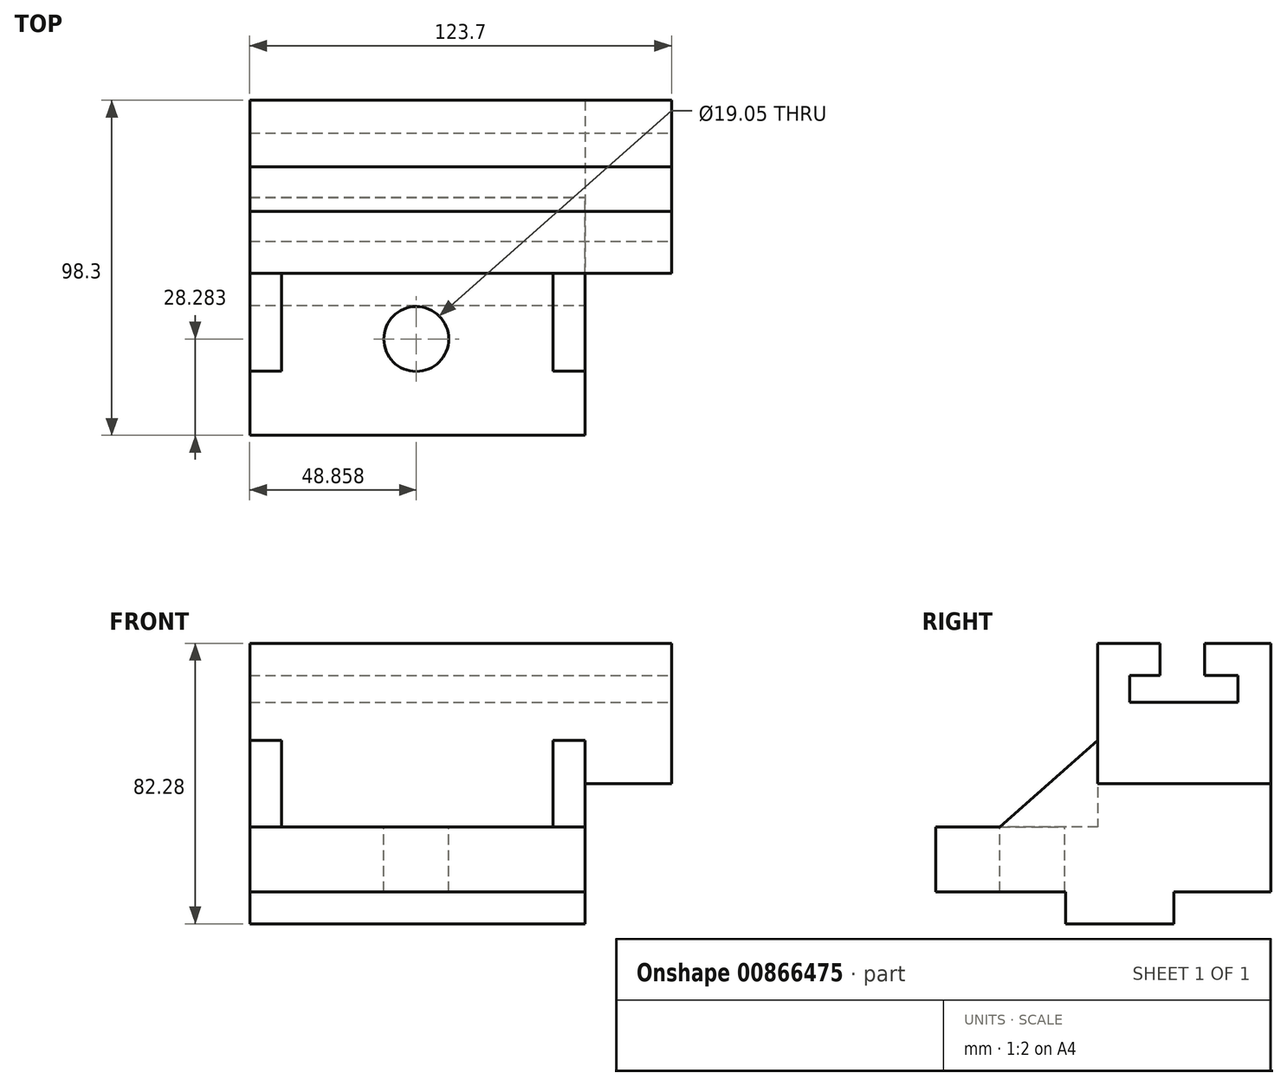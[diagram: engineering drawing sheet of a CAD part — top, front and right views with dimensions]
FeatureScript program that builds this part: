
annotation { "Feature Type Name" : "Feature", "Feature Type Description" : "" }
export const myFeature = defineFeature(function(context is Context, id is Id, definition is map)
    precondition{}
    {
        {
            var Q0;
            Q0=qCreatedBy(makeId("Top.planeOp"),FACE);
            var sketch = newSketch(context, id + "F0", { "sketchPlane" : qUnion([Q0])});
            skLineSegment(sketch, "E0.bottom", {"start": v(-46.6, 79.5) * mm, "end": v(51.7, 79.5) * mm});
            skLineSegment(sketch, "E0.top", {"start": v(-46.6, -18.8) * mm, "end": v(51.7, -18.8) * mm});
            skLineSegment(sketch, "E0.left", {"start": v(-46.6, 79.5) * mm, "end": v(-46.6, -18.8) * mm});
            skLineSegment(sketch, "E0.right", {"start": v(51.7, 79.5) * mm, "end": v(51.7, -18.8) * mm});
            skLineSegment(sketch, "E1", {"start": v(-46.6, 79.5) * mm, "end": v(-46.6, 30.35) * mm});
            skLineSegment(sketch, "E2", {"start": v(-46.6, 30.35) * mm, "end": v(-46.6, -1.4) * mm});
            skSolve(sketch);
        }
        {
            var Q0;
            Q0=makeQuery(id+"F0.imprint","IMPRINT",FACE,{"disambiguationData":[TD([[makeQuery(id+"F0.imprint","IMPRINT",EDGE,{"derivedFrom":sQuery(id+"F0.wireOp",EDGE,"E0.bottom")}),-1.0]])]});
            extrude(context, id + "F1", {"entities" : qUnion([Q0]), "depth" : 19.05 * mm, "offsetDistance" : 25.4 * mm});
        }
        {
            var Q0;
            Q0=makeQuery(id+"F1.opExtrude","SWEPT_FACE",FACE,{"disambiguationData":[OSD([sQuery(id+"F0.wireOp",EDGE,"E0.right")])]});
            var sketch = newSketch(context, id + "F2", { "sketchPlane" : qUnion([Q0])});
            skLineSegment(sketch, "E3", {"start": v(79.5, 0) * mm, "end": v(51.05, 0) * mm});
            skLineSegment(sketch, "E4", {"start": v(51.05, 0) * mm, "end": v(19.3, 0) * mm});
            skLineSegment(sketch, "E5", {"start": v(19.3, 0) * mm, "end": v(19.3, -9.38) * mm});
            skLineSegment(sketch, "E6", {"start": v(19.3, -9.38) * mm, "end": v(51.02, -9.38) * mm});
            skLineSegment(sketch, "E7", {"start": v(51.02, -9.38) * mm, "end": v(51.05, 0) * mm});
            skSolve(sketch);
        }
        {
            var Q0;
            Q0=makeQuery(id+"F2.imprint","IMPRINT",FACE,{"disambiguationData":[TD([[makeQuery(id+"F2.imprint","IMPRINT",EDGE,{"derivedFrom":sQuery(id+"F2.wireOp",EDGE,"E4")}),1.0]])]});
            extrude(context, id + "F3", {"entities" : qUnion([Q0]), "operationType" : NewBodyOperationType.ADD, "oppositeDirection" : true, "depth" : 98.3 * mm, "offsetDistance" : 25.4 * mm});
        }
        {
            var Q0;
            Q0=makeQuery(id+"F1.opExtrude","CAP_FACE",FACE,{"disambiguationData":[OSD([sQuery(id+"F0.wireOp",EDGE,"E0.bottom"),sQuery(id+"F0.wireOp",EDGE,"E0.top"),sQuery(id+"F0.wireOp",EDGE,"E0.left"),sQuery(id+"F0.wireOp",EDGE,"E0.right"),sQuery(id+"F0.wireOp",EDGE,"E1"),sQuery(id+"F0.wireOp",EDGE,"E2")])],"isStart":false});
            var sketch = newSketch(context, id + "F4", { "sketchPlane" : qUnion([Q0])});
            skLineSegment(sketch, "E8.bottom", {"start": v(-46.6, 79.5) * mm, "end": v(77.1, 79.5) * mm});
            skLineSegment(sketch, "E8.top", {"start": v(-46.6, 28.7) * mm, "end": v(77.1, 28.7) * mm});
            skLineSegment(sketch, "E8.left", {"start": v(-46.6, 79.5) * mm, "end": v(-46.6, 28.7) * mm});
            skLineSegment(sketch, "E8.right", {"start": v(77.1, 79.5) * mm, "end": v(77.1, 28.7) * mm});
            skSolve(sketch);
        }
        {
            var Q0;
            Q0 = qSketchRegion(id + "F4", true);
            extrude(context, id + "F5", {"entities" : qUnion([Q0]), "operationType" : NewBodyOperationType.ADD, "depth" : 53.85 * mm, "offsetDistance" : 25.4 * mm});
        }
        {
            var Q0;
            Q0=makeQuery(id+"F1.opExtrude","CAP_FACE",FACE,{"disambiguationData":[OSD([sQuery(id+"F0.wireOp",EDGE,"E0.bottom"),sQuery(id+"F0.wireOp",EDGE,"E0.top"),sQuery(id+"F0.wireOp",EDGE,"E0.left"),sQuery(id+"F0.wireOp",EDGE,"E0.right"),sQuery(id+"F0.wireOp",EDGE,"E1"),sQuery(id+"F0.wireOp",EDGE,"E2")])],"isStart":false});
            var sketch = newSketch(context, id + "F6", { "sketchPlane" : qUnion([Q0])});
            skLineSegment(sketch, "E9.bottom", {"start": v(51.7, 28.7) * mm, "end": v(42.3, 28.7) * mm});
            skLineSegment(sketch, "E9.top", {"start": v(51.7, 0) * mm, "end": v(42.3, 0) * mm});
            skLineSegment(sketch, "E9.left", {"start": v(51.7, 28.7) * mm, "end": v(51.7, 0) * mm});
            skLineSegment(sketch, "E9.right", {"start": v(42.3, 28.7) * mm, "end": v(42.3, 0) * mm});
            skSolve(sketch);
        }
        {
            var Q0;
            Q0 = qSketchRegion(id + "F6", true);
            extrude(context, id + "F7", {"entities" : qUnion([Q0]), "operationType" : NewBodyOperationType.ADD, "depth" : 25.4 * mm, "offsetDistance" : 25.4 * mm});
        }
        {
            var Q0;
            Q0=makeQuery(id+"F7.boolean.opBoolean","MERGE",FACE,{"derivedFrom":[makeQuery(id+"F3.boolean.opBoolean","MERGE",FACE,{"derivedFrom":[makeQuery(id+"F1.opExtrude","SWEPT_FACE",FACE,{"disambiguationData":[OSD([sQuery(id+"F0.wireOp",EDGE,"E0.right")])]}),makeQuery(id+"F3.opExtrude","CAP_FACE",FACE,{"disambiguationData":[OSD([sQuery(id+"F2.wireOp",EDGE,"E4"),sQuery(id+"F2.wireOp",EDGE,"E5"),sQuery(id+"F2.wireOp",EDGE,"E6"),sQuery(id+"F2.wireOp",EDGE,"E7")])],"isStart":true})]}),makeQuery(id+"F7.opExtrude","SWEPT_FACE",FACE,{"disambiguationData":[OSD([sQuery(id+"F6.wireOp",EDGE,"E9.left")])]})]});
            var sketch = newSketch(context, id + "F8", { "sketchPlane" : qUnion([Q0])});
            skLineSegment(sketch, "E10", {"start": v(0, 19.05) * mm, "end": v(28.7, 44.45) * mm});
            skSolve(sketch);
        }
        {
            var Q0;
            Q0 = qSketchRegion(id + "F8", true);
            var Q1;
            Q1=makeQuery(id+"F8.imprint","IMPRINT",FACE,{"disambiguationData":[TD([[makeQuery(id+"F8.imprint","IMPRINT",EDGE,{"derivedFrom":sQuery(id+"F8.wireOp",EDGE,"E10")}),1.0]])]});
            extrude(context, id + "F9", {"entities" : qUnion([Q0, Q1]), "operationType" : NewBodyOperationType.REMOVE, "oppositeDirection" : true, "depth" : 25.4 * mm, "offsetDistance" : 25.4 * mm});
        }
        {
            var Q0;
            Q0=makeQuery(id+"F1.opExtrude","CAP_FACE",FACE,{"disambiguationData":[OSD([sQuery(id+"F0.wireOp",EDGE,"E0.bottom"),sQuery(id+"F0.wireOp",EDGE,"E0.top"),sQuery(id+"F0.wireOp",EDGE,"E0.left"),sQuery(id+"F0.wireOp",EDGE,"E0.right"),sQuery(id+"F0.wireOp",EDGE,"E1"),sQuery(id+"F0.wireOp",EDGE,"E2")])],"isStart":false});
            var sketch = newSketch(context, id + "F10", { "sketchPlane" : qUnion([Q0])});
            skLineSegment(sketch, "E11.bottom", {"start": v(-46.6, 28.7) * mm, "end": v(-37.2, 28.7) * mm});
            skLineSegment(sketch, "E11.top", {"start": v(-46.6, 0) * mm, "end": v(-37.2, 0) * mm});
            skLineSegment(sketch, "E11.left", {"start": v(-46.6, 28.7) * mm, "end": v(-46.6, 0) * mm});
            skLineSegment(sketch, "E11.right", {"start": v(-37.2, 28.7) * mm, "end": v(-37.2, 0) * mm});
            skSolve(sketch);
        }
        {
            var Q0;
            Q0 = qSketchRegion(id + "F10", true);
            extrude(context, id + "F11", {"entities" : qUnion([Q0]), "operationType" : NewBodyOperationType.ADD, "depth" : 25.4 * mm, "offsetDistance" : 25.4 * mm});
        }
        {
            var Q0;
            Q0=makeQuery(id+"F11.boolean.opBoolean","MERGE",FACE,{"derivedFrom":[makeQuery(id+"F5.boolean.opBoolean","MERGE",FACE,{"derivedFrom":[makeQuery(id+"F3.boolean.opBoolean","MERGE",FACE,{"derivedFrom":[makeQuery(id+"F1.opExtrude","SWEPT_FACE",FACE,{"disambiguationData":[OSD([sQuery(id+"F0.wireOp",EDGE,"E0.left"),sQuery(id+"F0.wireOp",EDGE,"E1"),sQuery(id+"F0.wireOp",EDGE,"E2")])]}),makeQuery(id+"F3.opExtrude","CAP_FACE",FACE,{"disambiguationData":[OSD([sQuery(id+"F2.wireOp",EDGE,"E4"),sQuery(id+"F2.wireOp",EDGE,"E5"),sQuery(id+"F2.wireOp",EDGE,"E6"),sQuery(id+"F2.wireOp",EDGE,"E7")])],"isStart":false})]}),makeQuery(id+"F5.opExtrude","SWEPT_FACE",FACE,{"disambiguationData":[OSD([sQuery(id+"F4.wireOp",EDGE,"E8.left")])]})]}),makeQuery(id+"F11.opExtrude","SWEPT_FACE",FACE,{"disambiguationData":[OSD([sQuery(id+"F10.wireOp",EDGE,"E11.left")])]})]});
            var sketch = newSketch(context, id + "F12", { "sketchPlane" : qUnion([Q0])});
            skLineSegment(sketch, "E12", {"start": v(0, 19.05) * mm, "end": v(-28.7, 44.45) * mm});
            skSolve(sketch);
        }
        {
            var Q0;
            Q0 = qSketchRegion(id + "F12", true);
            var Q1;
            Q1=makeQuery(id+"F12.imprint","IMPRINT",FACE,{"disambiguationData":[TD([[makeQuery(id+"F12.imprint","IMPRINT",EDGE,{"derivedFrom":sQuery(id+"F12.wireOp",EDGE,"E12")}),-1.0]])]});
            extrude(context, id + "F13", {"entities" : qUnion([Q0, Q1]), "operationType" : NewBodyOperationType.REMOVE, "oppositeDirection" : true, "depth" : 25.4 * mm, "offsetDistance" : 25.4 * mm});
        }
        {
            var Q0;
            Q0=makeQuery(id+"F1.opExtrude","CAP_FACE",FACE,{"disambiguationData":[OSD([sQuery(id+"F0.wireOp",EDGE,"E0.bottom"),sQuery(id+"F0.wireOp",EDGE,"E0.top"),sQuery(id+"F0.wireOp",EDGE,"E0.left"),sQuery(id+"F0.wireOp",EDGE,"E0.right"),sQuery(id+"F0.wireOp",EDGE,"E1"),sQuery(id+"F0.wireOp",EDGE,"E2")])],"isStart":false});
            var sketch = newSketch(context, id + "F14", { "sketchPlane" : qUnion([Q0])});
            skCircle(sketch, "E13", {"center": v(2.26, 9.48) * mm, "radius": 9.53 * mm});
            skSolve(sketch);
        }
        {
            var Q0;
            Q0=makeQuery(id+"F14.imprint","IMPRINT",FACE,{"disambiguationData":[TD([[makeQuery(id+"F14.imprint","IMPRINT",EDGE,{"derivedFrom":sQuery(id+"F14.wireOp",EDGE,"E13")}),1.0]])]});
            extrude(context, id + "F15", {"entities" : qUnion([Q0]), "operationType" : NewBodyOperationType.REMOVE, "oppositeDirection" : true, "depth" : 25.4 * mm, "offsetDistance" : 25.4 * mm});
        }
        {
            var Q0;
            Q0=makeQuery(id+"F5.opExtrude","SWEPT_FACE",FACE,{"disambiguationData":[OSD([sQuery(id+"F4.wireOp",EDGE,"E8.right")])]});
            var sketch = newSketch(context, id + "F16", { "sketchPlane" : qUnion([Q0])});
            skLineSegment(sketch, "E14", {"start": v(46.96, 72.9) * mm, "end": v(46.96, 63.5) * mm});
            skLineSegment(sketch, "E15", {"start": v(46.96, 63.5) * mm, "end": v(38.1, 63.5) * mm});
            skLineSegment(sketch, "E16", {"start": v(38.1, 63.5) * mm, "end": v(38.1, 55.63) * mm});
            skLineSegment(sketch, "E17", {"start": v(38.1, 55.63) * mm, "end": v(69.86, 55.63) * mm});
            skLineSegment(sketch, "E18", {"start": v(69.86, 55.63) * mm, "end": v(69.86, 63.5) * mm});
            skLineSegment(sketch, "E19", {"start": v(69.86, 63.5) * mm, "end": v(60, 63.5) * mm});
            skLineSegment(sketch, "E20", {"start": v(60, 63.5) * mm, "end": v(60, 72.9) * mm});
            skLineSegment(sketch, "E21", {"start": v(60, 72.9) * mm, "end": v(46.96, 72.9) * mm});
            skSolve(sketch);
        }
        {
            var Q0;
            Q0=makeQuery(id+"F16.imprint","IMPRINT",FACE,{"disambiguationData":[TD([[makeQuery(id+"F16.imprint","IMPRINT",EDGE,{"derivedFrom":sQuery(id+"F16.wireOp",EDGE,"E14")}),1.0]])]});
            extrude(context, id + "F17", {"entities" : qUnion([Q0]), "operationType" : NewBodyOperationType.REMOVE, "oppositeDirection" : true, "depth" : 227.84 * mm, "offsetDistance" : 25.4 * mm});
        }
        {
            var Q0;
            Q0=makeQuery(id+"F5.opExtrude","CAP_FACE",FACE,{"disambiguationData":[OSD([sQuery(id+"F4.wireOp",EDGE,"E8.bottom"),sQuery(id+"F4.wireOp",EDGE,"E8.top"),sQuery(id+"F4.wireOp",EDGE,"E8.left"),sQuery(id+"F4.wireOp",EDGE,"E8.right")])],"isStart":true});
            extrude(context, id + "F18", {"entities" : qUnion([Q0]), "operationType" : NewBodyOperationType.ADD, "oppositeDirection" : true, "depth" : 12.7 * mm, "offsetDistance" : 25.4 * mm});
        }
        {
            var Q0;
            Q0=makeQuery(id+"F5.opExtrude","CAP_FACE",FACE,{"disambiguationData":[OSD([sQuery(id+"F4.wireOp",EDGE,"E8.bottom"),sQuery(id+"F4.wireOp",EDGE,"E8.top"),sQuery(id+"F4.wireOp",EDGE,"E8.left"),sQuery(id+"F4.wireOp",EDGE,"E8.right")])],"isStart":true});
            var sketch = newSketch(context, id + "F19", { "sketchPlane" : qUnion([Q0])});
            skSolve(sketch);
        }
        {
            var Q0;
            Q0 = qSketchRegion(id + "F19", true);
            var Q1;
            {var subQ0=sQuery(id+"F4.wireOp",EDGE,"E8.right");Q1=makeQuery(id+"F19.imprint","IMPRINT",FACE,{"disambiguationData":[TD([[makeQuery(id+"F19.imprint","IMPRINT",EDGE,{"derivedFrom":makeQuery(id+"F5.opExtrude","CAP_EDGE",EDGE,{"disambiguationData":[OSD([subQ0])],"isStart":true})}),1.0]])]});}
            extrude(context, id + "F20", {"entities" : qUnion([Q0, Q1]), "operationType" : NewBodyOperationType.REMOVE, "oppositeDirection" : true, "depth" : 12.7 * mm, "offsetDistance" : 25.4 * mm});
        }
    });
